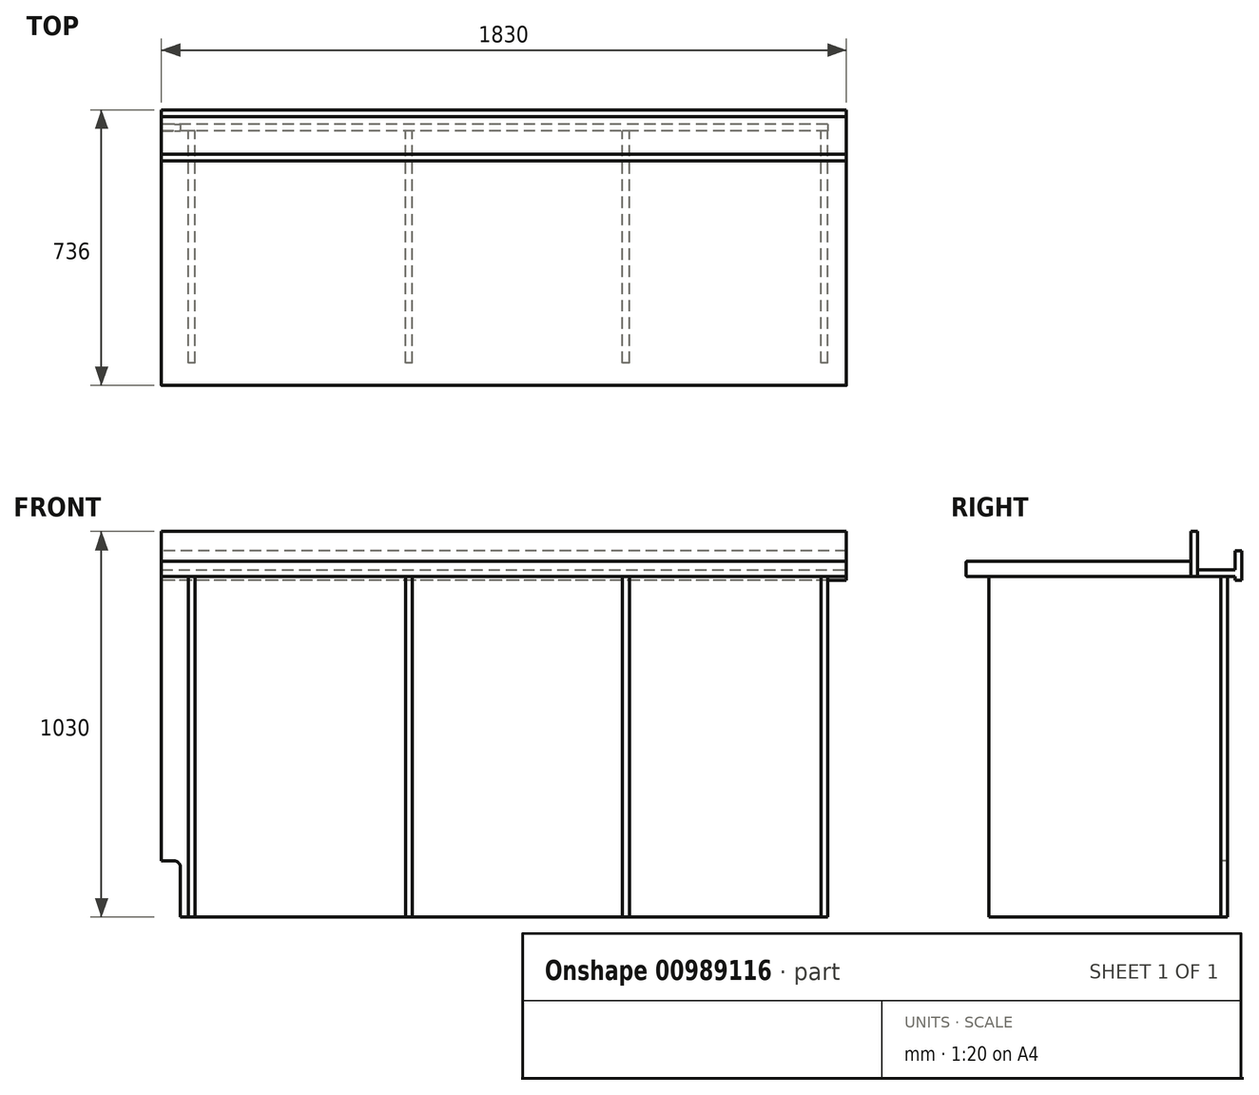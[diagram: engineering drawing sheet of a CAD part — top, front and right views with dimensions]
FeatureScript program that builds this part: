
annotation { "Feature Type Name" : "Feature", "Feature Type Description" : "" }
export const myFeature = defineFeature(function(context is Context, id is Id, definition is map)
    precondition{}
    {
        {
            var Q0;
            Q0=qCreatedBy(makeId("Right.planeOp"),FACE);
            var sketch = newSketch(context, id + "F0", { "sketchPlane" : qUnion([Q0])});
            skLineSegment(sketch, "E0", {"start": v(600, 0) * mm, "end": v(600, -40) * mm});
            skLineSegment(sketch, "E1", {"start": v(600, -40) * mm, "end": v(0, -40) * mm});
            skLineSegment(sketch, "E2", {"start": v(0, -40) * mm, "end": v(0, 1) * mm});
            skLineSegment(sketch, "E3", {"start": v(5, 0) * mm, "end": v(600, 0) * mm});
            skLineSegment(sketch, "E4", {"start": v(5, 0) * mm, "end": v(0, 1) * mm});
            skSolve(sketch);
        }
        {
            var Q0;
            Q0 = qSketchRegion(id + "F0", true);
            extrude(context, id + "F1", {"entities" : qUnion([Q0]), "depth" : 1830 * mm, "offsetDistance" : 25 * mm});
        }
        {
            var Q0;
            Q0=makeQuery(id+"F1.opExtrude","SWEPT_EDGE",EDGE,{"disambiguationData":[OSD([sQuery(id+"F0.wireOp",EDGE,"E2"),sQuery(id+"F0.wireOp",EDGE,"E4")])]});
            var Q1;
            Q1=makeQuery(id+"F1.opExtrude","SWEPT_EDGE",EDGE,{"disambiguationData":[OSD([sQuery(id+"F0.wireOp",EDGE,"E1"),sQuery(id+"F0.wireOp",EDGE,"E2")])]});
            fillet(context, id + "F2", {"entities" : qUnion([Q0, Q1]), "radius" : 2.5 * mm, "tangentPropagation" : true, "allowEdgeOverflow" : false});
        }
        {
            var Q0;
            Q0=makeQuery(id+"F1.opExtrude","SWEPT_EDGE",EDGE,{"disambiguationData":[OSD([sQuery(id+"F0.wireOp",EDGE,"E3"),sQuery(id+"F0.wireOp",EDGE,"E4")])]});
            fillet(context, id + "F3", {"entities" : qUnion([Q0]), "radius" : 20 * mm, "tangentPropagation" : true, "allowEdgeOverflow" : false});
        }
        {
            var Q0;
            Q0=qCreatedBy(makeId("Right.planeOp"),FACE);
            cPlane(context, id + "F4", {"entities" : qUnion([Q0]), "cplaneType" : CPlaneType.OFFSET, "offset" : 1762 * mm, "width" : 150 * mm, "height" : 150 * mm});
        }
        {
            var Q0;
            Q0=qCreatedBy(id+"F4.planeOp",FACE);
            var sketch = newSketch(context, id + "F5", { "sketchPlane" : qUnion([Q0])});
            skLineSegment(sketch, "E5.bottom", {"start": v(60, -40) * mm, "end": v(680, -40) * mm});
            skLineSegment(sketch, "E5.top", {"start": v(60, -950) * mm, "end": v(680, -950) * mm});
            skLineSegment(sketch, "E5.left", {"start": v(60, -40) * mm, "end": v(60, -950) * mm});
            skLineSegment(sketch, "E5.right", {"start": v(680, -40) * mm, "end": v(680, -950) * mm});
            skSolve(sketch);
        }
        {
            var Q0;
            Q0 = qSketchRegion(id + "F5", true);
            extrude(context, id + "F6", {"entities" : qUnion([Q0]), "oppositeDirection" : true, "depth" : -18 * mm, "offsetDistance" : 25 * mm});
        }
        {
            var Q0;
            Q0=qCreatedBy(id+"F4.planeOp",FACE);
            cPlane(context, id + "F7", {"entities" : qUnion([Q0]), "cplaneType" : CPlaneType.OFFSET, "offset" : 530 * mm, "oppositeDirection" : true, "width" : 150 * mm, "height" : 150 * mm});
        }
        {
            var Q0;
            Q0=qCreatedBy(id+"F7.planeOp",FACE);
            var sketch = newSketch(context, id + "F8", { "sketchPlane" : qUnion([Q0])});
            skLineSegment(sketch, "E6.bottom", {"start": v(60, -40) * mm, "end": v(680, -40) * mm});
            skLineSegment(sketch, "E6.top", {"start": v(60, -950) * mm, "end": v(680, -950) * mm});
            skLineSegment(sketch, "E6.left", {"start": v(60, -40) * mm, "end": v(60, -950) * mm});
            skLineSegment(sketch, "E6.right", {"start": v(680, -40) * mm, "end": v(680, -950) * mm});
            skSolve(sketch);
        }
        {
            var Q0;
            Q0=makeQuery(id+"F8.imprint","IMPRINT",FACE,{"disambiguationData":[TD([[makeQuery(id+"F8.imprint","IMPRINT",EDGE,{"derivedFrom":sQuery(id+"F8.wireOp",EDGE,"E6.bottom")}),-1.0]])]});
            extrude(context, id + "F9", {"entities" : qUnion([Q0]), "depth" : 18 * mm, "offsetDistance" : 25 * mm});
        }
        {
            var Q0;
            Q0=qCreatedBy(id+"F7.planeOp",FACE);
            cPlane(context, id + "F10", {"entities" : qUnion([Q0]), "cplaneType" : CPlaneType.OFFSET, "offset" : 580 * mm, "oppositeDirection" : true, "width" : 150 * mm, "height" : 150 * mm});
        }
        {
            var Q0;
            Q0=qCreatedBy(id+"F10.planeOp",FACE);
            var sketch = newSketch(context, id + "F11", { "sketchPlane" : qUnion([Q0])});
            skLineSegment(sketch, "E7.bottom", {"start": v(60, -40) * mm, "end": v(680, -40) * mm});
            skLineSegment(sketch, "E7.top", {"start": v(60, -950) * mm, "end": v(680, -950) * mm});
            skLineSegment(sketch, "E7.left", {"start": v(60, -40) * mm, "end": v(60, -950) * mm});
            skLineSegment(sketch, "E7.right", {"start": v(680, -40) * mm, "end": v(680, -950) * mm});
            skSolve(sketch);
        }
        {
            var Q0;
            Q0 = qSketchRegion(id + "F11", true);
            extrude(context, id + "F12", {"entities" : qUnion([Q0]), "depth" : 18 * mm, "offsetDistance" : 25 * mm});
        }
        {
            var Q0;
            Q0=qCreatedBy(id+"F10.planeOp",FACE);
            cPlane(context, id + "F13", {"entities" : qUnion([Q0]), "cplaneType" : CPlaneType.OFFSET, "offset" : 580 * mm, "oppositeDirection" : true, "width" : 150 * mm, "height" : 150 * mm});
        }
        {
            var Q0;
            Q0=qCreatedBy(id+"F13.planeOp",FACE);
            var sketch = newSketch(context, id + "F14", { "sketchPlane" : qUnion([Q0])});
            skLineSegment(sketch, "E8.bottom", {"start": v(60, -40) * mm, "end": v(680, -40) * mm});
            skLineSegment(sketch, "E8.top", {"start": v(60, -950) * mm, "end": v(680, -950) * mm});
            skLineSegment(sketch, "E8.left", {"start": v(60, -40) * mm, "end": v(60, -950) * mm});
            skLineSegment(sketch, "E8.right", {"start": v(680, -40) * mm, "end": v(680, -950) * mm});
            skSolve(sketch);
        }
        {
            var Q0;
            Q0 = qSketchRegion(id + "F14", true);
            extrude(context, id + "F15", {"entities" : qUnion([Q0]), "depth" : 18 * mm, "offsetDistance" : 25 * mm});
        }
        {
            var Q0;
            Q0=makeQuery(id+"F6.opExtrude","SWEPT_FACE",FACE,{"disambiguationData":[OSD([sQuery(id+"F5.wireOp",EDGE,"E5.right")])]});
            cPlane(context, id + "F16", {"entities" : qUnion([Q0]), "cplaneType" : CPlaneType.OFFSET, "offset" : 0 * mm, "width" : 150 * mm, "height" : 150 * mm});
        }
        {
            var Q0;
            Q0=qCreatedBy(id+"F16.planeOp",FACE);
            var sketch = newSketch(context, id + "F17", { "sketchPlane" : qUnion([Q0])});
            skLineSegment(sketch, "E9.bottom", {"start": v(-1780, -40) * mm, "end": v(0, -40) * mm});
            skLineSegment(sketch, "E9.top", {"start": v(-1780, -950) * mm, "end": v(0, -950) * mm});
            skLineSegment(sketch, "E9.left", {"start": v(-1780, -40) * mm, "end": v(-1780, -950) * mm});
            skLineSegment(sketch, "E9.right", {"start": v(0, -40) * mm, "end": v(0, -950) * mm});
            skSolve(sketch);
        }
        {
            var Q0;
            Q0 = qSketchRegion(id + "F17", true);
            extrude(context, id + "F18", {"entities" : qUnion([Q0]), "depth" : 18 * mm, "offsetDistance" : 25 * mm});
        }
        {
            var Q0;
            Q0=makeQuery(id+"F1.opExtrude","SWEPT_FACE",FACE,{"disambiguationData":[OSD([sQuery(id+"F0.wireOp",EDGE,"E0")])]});
            cPlane(context, id + "F19", {"entities" : qUnion([Q0]), "cplaneType" : CPlaneType.OFFSET, "offset" : 0 * mm, "width" : 150 * mm, "height" : 150 * mm});
        }
        {
            var Q0;
            Q0=qCreatedBy(id+"F19.planeOp",FACE);
            var sketch = newSketch(context, id + "F20", { "sketchPlane" : qUnion([Q0])});
            skLineSegment(sketch, "E10.bottom", {"start": v(0, -40) * mm, "end": v(-1830, -40) * mm});
            skLineSegment(sketch, "E10.top", {"start": v(0, 80) * mm, "end": v(-1830, 80) * mm});
            skLineSegment(sketch, "E10.left", {"start": v(0, -40) * mm, "end": v(0, 80) * mm});
            skLineSegment(sketch, "E10.right", {"start": v(-1830, -40) * mm, "end": v(-1830, 80) * mm});
            skSolve(sketch);
        }
        {
            var Q0;
            Q0 = qSketchRegion(id + "F20", true);
            extrude(context, id + "F21", {"entities" : qUnion([Q0]), "depth" : 18 * mm, "offsetDistance" : 25 * mm});
        }
        {
            var Q0;
            Q0=makeQuery(id+"F18.opExtrude","SWEPT_FACE",FACE,{"disambiguationData":[OSD([sQuery(id+"F17.wireOp",EDGE,"E9.bottom")])]});
            cPlane(context, id + "F22", {"entities" : qUnion([Q0]), "cplaneType" : CPlaneType.OFFSET, "offset" : 0 * mm, "width" : 150 * mm, "height" : 150 * mm});
        }
        {
            var Q0;
            Q0=qCreatedBy(id+"F22.planeOp",FACE);
            var sketch = newSketch(context, id + "F23", { "sketchPlane" : qUnion([Q0])});
            skLineSegment(sketch, "E11.bottom", {"start": v(0, 618) * mm, "end": v(1830, 618) * mm});
            skLineSegment(sketch, "E11.top", {"start": v(0, 718) * mm, "end": v(1830, 718) * mm});
            skLineSegment(sketch, "E11.left", {"start": v(0, 618) * mm, "end": v(0, 718) * mm});
            skLineSegment(sketch, "E11.right", {"start": v(1830, 618) * mm, "end": v(1830, 718) * mm});
            skSolve(sketch);
        }
        {
            var Q0;
            Q0 = qSketchRegion(id + "F23", true);
            extrude(context, id + "F24", {"entities" : qUnion([Q0]), "depth" : 18 * mm, "offsetDistance" : 25 * mm});
        }
        {
            var Q0;
            Q0=makeQuery(id+"F24.opExtrude","SWEPT_FACE",FACE,{"disambiguationData":[OSD([sQuery(id+"F23.wireOp",EDGE,"E11.top")])]});
            cPlane(context, id + "F25", {"entities" : qUnion([Q0]), "cplaneType" : CPlaneType.OFFSET, "offset" : 0 * mm, "width" : 150 * mm, "height" : 150 * mm});
        }
        {
            var Q0;
            Q0=qCreatedBy(id+"F25.planeOp",FACE);
            var sketch = newSketch(context, id + "F26", { "sketchPlane" : qUnion([Q0])});
            skLineSegment(sketch, "E12.bottom", {"start": v(-1830, -50) * mm, "end": v(0, -50) * mm});
            skLineSegment(sketch, "E12.top", {"start": v(-1830, 28) * mm, "end": v(0, 28) * mm});
            skLineSegment(sketch, "E12.left", {"start": v(-1830, -50) * mm, "end": v(-1830, 28) * mm});
            skLineSegment(sketch, "E12.right", {"start": v(0, -50) * mm, "end": v(0, 28) * mm});
            skSolve(sketch);
        }
        {
            var Q0;
            Q0 = qSketchRegion(id + "F26", true);
            extrude(context, id + "F27", {"entities" : qUnion([Q0]), "operationType" : NewBodyOperationType.ADD, "depth" : 18 * mm, "offsetDistance" : 25 * mm});
        }
        {
            var Q0;
            Q0=makeQuery(id+"F18.opExtrude","CAP_FACE",FACE,{"disambiguationData":[OSD([sQuery(id+"F17.wireOp",EDGE,"E9.bottom"),sQuery(id+"F17.wireOp",EDGE,"E9.top"),sQuery(id+"F17.wireOp",EDGE,"E9.left"),sQuery(id+"F17.wireOp",EDGE,"E9.right")])],"isStart":true});
            cPlane(context, id + "F28", {"entities" : qUnion([Q0]), "cplaneType" : CPlaneType.OFFSET, "offset" : 0 * mm, "width" : 150 * mm, "height" : 150 * mm});
        }
        {
            var Q0;
            Q0=qCreatedBy(id+"F28.planeOp",FACE);
            var sketch = newSketch(context, id + "F29", { "sketchPlane" : qUnion([Q0])});
            skLineSegment(sketch, "E13.bottom", {"start": v(0, -950) * mm, "end": v(50, -950) * mm});
            skLineSegment(sketch, "E13.top", {"start": v(0, -800) * mm, "end": v(50, -800) * mm});
            skLineSegment(sketch, "E13.left", {"start": v(0, -950) * mm, "end": v(0, -800) * mm});
            skLineSegment(sketch, "E13.right", {"start": v(50, -950) * mm, "end": v(50, -800) * mm});
            skSolve(sketch);
        }
        {
            var Q0;
            Q0 = qSketchRegion(id + "F29", true);
            extrude(context, id + "F30", {"entities" : qUnion([Q0]), "operationType" : NewBodyOperationType.REMOVE, "endBound" : BoundingType.THROUGH_ALL, "oppositeDirection" : true, "depth" : 25 * mm, "offsetDistance" : 25 * mm});
        }
        {
            var Q0;
            Q0=makeQuery(id+"F30.boolean.opBoolean","COPY",EDGE,{"derivedFrom":makeQuery(id+"F30.opExtrude","SWEPT_EDGE",EDGE,{"disambiguationData":[OSD([sQuery(id+"F29.wireOp",EDGE,"E13.top"),sQuery(id+"F29.wireOp",EDGE,"E13.right")])]})});
            var Q1;
            Q1=makeQuery(id+"F30.boolean.opBoolean","COPY",EDGE,{"derivedFrom":makeQuery(id+"F30.opExtrude","SWEPT_EDGE",EDGE,{"disambiguationData":[OSD([sQuery(id+"F29.wireOp",EDGE,"E13.top"),sQuery(id+"F29.wireOp",EDGE,"E13.left")])]})});
            fillet(context, id + "F31", {"entities" : qUnion([Q0, Q1]), "radius" : 15 * mm, "tangentPropagation" : true, "allowEdgeOverflow" : false});
        }
    });
